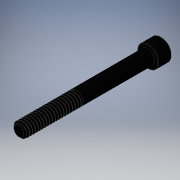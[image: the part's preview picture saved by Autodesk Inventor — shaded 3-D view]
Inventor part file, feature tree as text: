
AUTODESK INVENTOR PART (.ipt)
format: ipt  version: 2016 (Build 200138000, 138)  size: 552,448 bytes
history: native  units: in
note: dims shown in document units (in); Inventor stores cm internally (conversion verified against a paired STEP export)
features: chamfer x1
ambient origin geometry x8: Origin, YZ Plane, XZ Plane, XY Plane, X Axis, Y Axis, Z Axis, Center Point
bodies: Solid1 (feature_tree)
feature tree (1):
  chamfer  "Chamfer2"  [1 undecoded]
note: 1 required parameter value undecoded (feature->parameter linkage not recoverable at this tier; creation-order binding heuristic only, values carry confidence <= 0.55)
